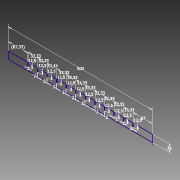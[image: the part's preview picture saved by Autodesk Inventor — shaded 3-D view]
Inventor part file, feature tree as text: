
AUTODESK INVENTOR PART (.ipt)
format: ipt  version: 2014 SP2 (Build 180246200, 246)  size: 108,032 bytes
history: native  units: mm
features: sketch x1
ambient origin geometry x8: Origin, YZ Plane, XZ Plane, XY Plane, X Axis, Y Axis, Z Axis, Center Point
feature tree (1):
  sketch  "Skizze1"  dims[d5=503.0mm d6=25.0mm d13=12.5mm d14=2.0mm d17=67.0mm d18=2.0mm d19=33.33mm d20=12.5mm d21=33.33mm d22=2.0mm d23=12.5mm d24=12.5mm d25=2.0mm d26=33.33mm d27=33.33mm d28=2.0mm d29=12.5mm d30=2.0mm d31=2.0mm d32=2.0mm d33=2.0mm d34=2.0mm d35=2.0mm d36=12.5mm d37=33.33mm d38=33.33mm d39=12.5mm d40=12.5mm d41=33.33mm d42=12.5mm d43=33.33mm d44=33.33mm d45=12.5mm d46=33.33mm d47=12.5mm d48=2.0mm d49=33.33mm d50=12.5mm d51=67.37mm]
